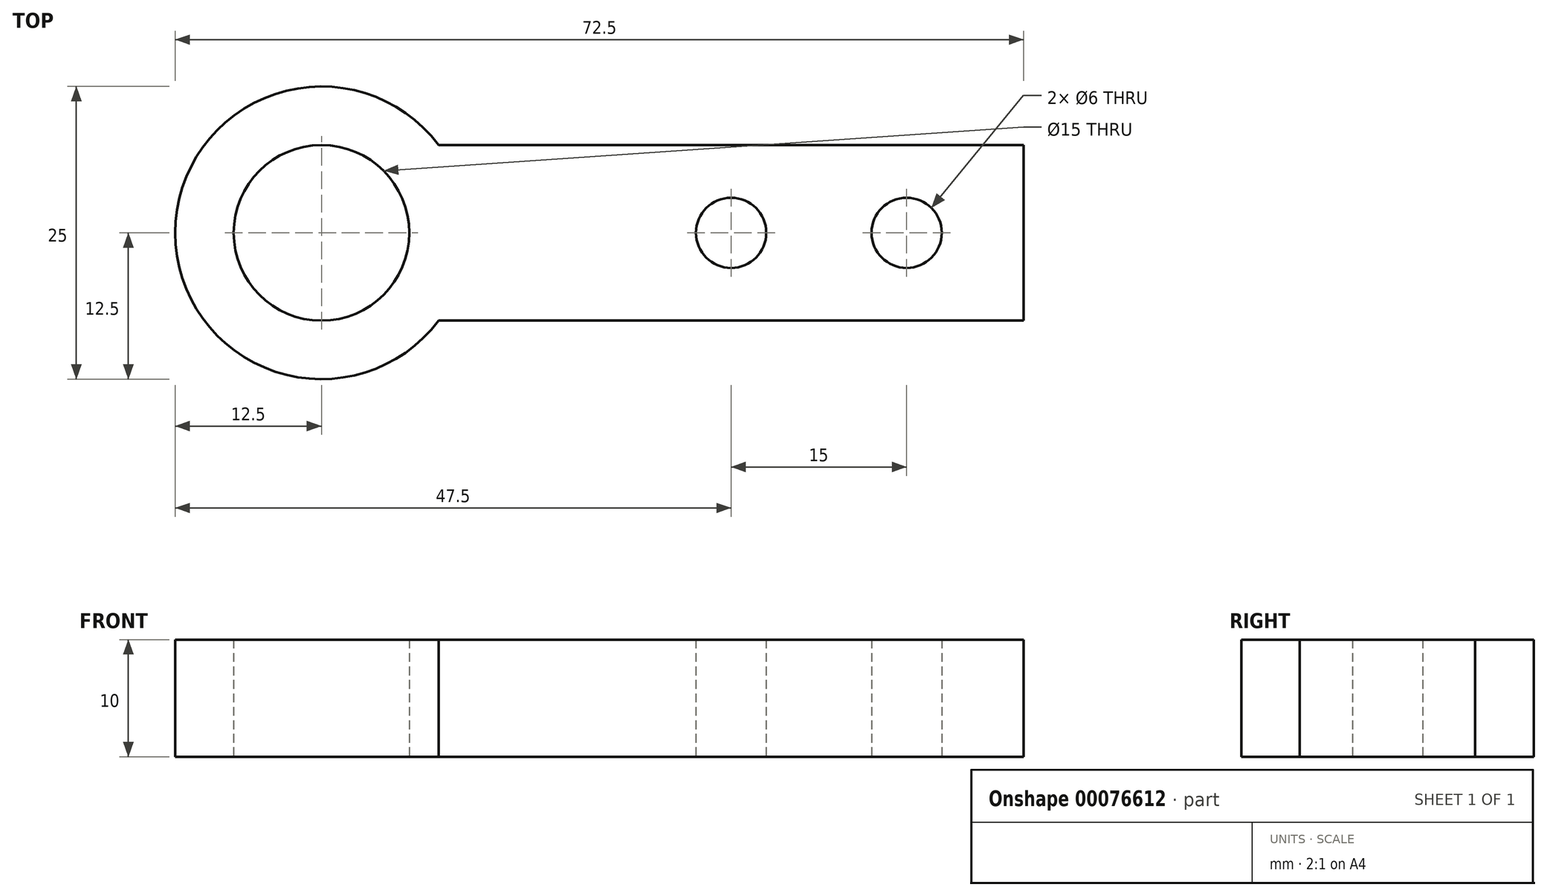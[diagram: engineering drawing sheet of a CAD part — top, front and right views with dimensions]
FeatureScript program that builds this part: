
annotation { "Feature Type Name" : "Feature", "Feature Type Description" : "" }
export const myFeature = defineFeature(function(context is Context, id is Id, definition is map)
    precondition{}
    {
        {
            var Q0;
            Q0=qCreatedBy(makeId("Top.planeOp"),FACE);
            var sketch = newSketch(context, id + "F0", { "sketchPlane" : qUnion([Q0])});
            skCircle(sketch, "E0", {"center": v(0, 0) * mm, "radius": 7.5 * mm});
            skCircle(sketch, "E1", {"center": v(0, 0) * mm, "radius": 12.5 * mm});
            skLineSegment(sketch, "E2", {"start": v(10, 7.5) * mm, "end": v(60, 7.5) * mm});
            skLineSegment(sketch, "E3", {"start": v(10, -7.5) * mm, "end": v(60, -7.5) * mm});
            skLineSegment(sketch, "E4", {"start": v(60, 7.5) * mm, "end": v(60, -7.5) * mm});
            skPoint(sketch, "E5.orphan", {"position": v(0, 7.5) * mm});
            skPoint(sketch, "E6.orphan", {"position": v(0, -7.5) * mm});
            skCircle(sketch, "E7", {"center": v(35, 0) * mm, "radius": 3 * mm});
            skCircle(sketch, "E8", {"center": v(50, 0) * mm, "radius": 3 * mm});
            skSolve(sketch);
        }
        {
            var Q0;
            Q0=makeQuery(id+"F0.imprint","IMPRINT",FACE,{"disambiguationData":[TD([[makeQuery(id+"F0.imprint","IMPRINT",EDGE,{"derivedFrom":sQuery(id+"F0.wireOp",EDGE,"E0")}),-1.0]])]});
            var Q1;
            {var subQ0=sQuery(id+"F0.wireOp",EDGE,"E2");Q1=makeQuery(id+"F0.imprint","IMPRINT",FACE,{"disambiguationData":[TD([[makeQuery(id+"F0.imprint","IMPRINT",EDGE,{"derivedFrom":subQ0}),-1.0]])]});}
            extrude(context, id + "F1", {"entities" : qUnion([Q0, Q1]), "depth" : 10 * mm});
        }
    });
